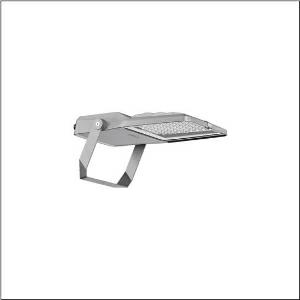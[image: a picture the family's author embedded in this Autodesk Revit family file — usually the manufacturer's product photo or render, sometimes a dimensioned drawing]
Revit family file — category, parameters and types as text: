
# Revit family: floodlight_fl_21_iq_mini___pl43_5xa7772c3a1a_2542
name_source: partatom
category: Lighting Fixtures
units: mm (PartAtom-declared; Revit-internal decimal feet)

## family parameters
Cut with Voids When Loaded = No
Host = Face
Light Source = No
Part Type = Normal
Room Calculation Point = No
Round Connector Dimension = Use Diameter
Shared = No

## types (1)
- --- (1 x LED, 10780 lm, 87.2 W, 3000K)
    Apparent Load = 87 VA
    CIE Flux Codes = 27 78 99 100 100
    Color Rendering = 80
    Color Temperature = 3000K
    Default Elevation = 1800 mm
    Description = Floodlight FL 21 iQ mini, floodlight, primary light control with lens, of PMMA, primary optical cover: protective disc, of toughened safety glass, transparent, light distribution: PL43, light emission: direct distribution, installation type: surface-mounted, lamps: LED, High Power LED, rated values: 10.780lm | 87,2W | 123,6lm/W (begin service life); end service life: 10.780lm | 92,1W; at 50% lumin. flux: 5.390lm | 40,1W | 134,4lm/W, colour temperature: 3000K, colour rendering: CRI > 80, light colour: 830, light setting 1 begin service life: 100% | 10.780lm | 87,2W | 123,6lm/W | 3.000K, light setting 1 end service life: 92,1W, further light settings possible, control: Street-Remote, Auto-Match, Temp-Guard, Night-Set, Smart-Wire, Desk-Remote (wireless, voltage-free reading and setting of iQ features in the workshop via application-optimized NFC function/RFID function), optimised constant luminous flux control (CLO 2.0), pre-setting: linear dimming characteristic, with terminal, 6-pole, mains connection: 220..240V, AC, 50/60Hz, luminaire housing, of diecast aluminium, powder-coated, SITECO metallic grey (DB 702S), corrosivity category C5 mid according to DIN EN ISO 12944suitable for swimming poolschlorine-resistant, sealing non-destructively replaceable, mounting bracket, of steel, galvanised, powder-coated, SITECO metallic grey (DB 702S), protection rating (complete): IP66, insulation class (complete): insulation class II (safety insulation), certification: CE, ENEC, VDE, protection symbol: D, impact resistance: IK08, permissible operating ambient temperature: -40..+40°C, permissible operating ambient temperature for outdoor applications: -40..+50°C, standard: DIN EN 12944, LABS conformity tested according to VDMA 24364:2018-05, packaging unit: 1 piece

Light Distribution: PL43
    Height = 70 mm
    Lamp = 1 x LED
    Lamp Light Flux = 10780 lm
    Lamp Power = 87.2 W
    Lamp count = 1
    Length = 485 mm
    Luminous efficacy = 124 lm/W
    Manufacturer = Siteco
    ModVariant = No
    Model = 5XA7772C3A1A
    Number of Poles = 1
    OnlyDefault = Yes
    Power Factor = 1
    Product Name = Floodlight FL 21 iQ mini | PL43
    Product group = floodlight | pylon annexe
    ProductGroupID = 6201
    Protection Class = Protection class II
    Protection Degree = IP 66
    RLX_Detail_Level = 1
    RLX_Emergency_Light_Flux = 0 lm
    RLX_Emergency_Type = 0
    RLX_Emergency_Type_DB = No
    RlxData = <blob elided: 96413 chars, md5=8337208d>
    Socket = socket
    Standby Power = 0 W
    System Light Flux = 10780 lm
    System Power = 87 W
    Type Comments = factory setting: luminous flux: 100 % | dim-lin: 254 | 456 mA
    Type Image = l_1006845.jpg
    URL = http://relux.com
    VarID = @adj_161731
    Voltage = 0 V
    Weight = 0.00 kg
    Width = 337 mm

## geometry (parser evidence)
native form markers: Blend x4, Sweep x12
no freeform markers — native parametric forms only
